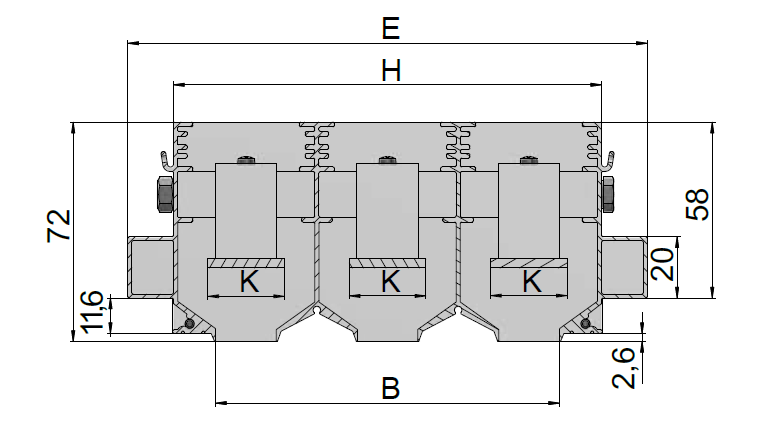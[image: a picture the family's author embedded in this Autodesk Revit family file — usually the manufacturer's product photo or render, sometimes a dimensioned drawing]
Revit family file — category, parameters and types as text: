
# Revit family: GR_Адаптер линейный_Муфта(n)_SDL-КСД-У_О_R21
name_source: partatom
category: Соединительные детали воздуховодов
units: mm (PartAtom-declared; Revit-internal decimal feet)

## family parameters
Всегда вертикально = Да
Заголовок OmniClass = Metal Ducts
На основе рабочей плоскости = Нет
Номер OmniClass = 23.75.70.14.31
Общий = Нет
При загрузке вырезать с полостями = Нет
Размер круглого соединителя = Использовать диаметр
Тип детали = Мультипорт

## types (6) — shared parameters
ADSK_URL страницы изделия = https://grilles.ru
ADSK_Версия Revit = 2021
ADSK_Единица измерения = шт.
ADSK_Завод-изготовитель = ООО "ВЕНТРЕШЕТКИКОМ"
ADSK_Код изделия = 000192
ADSK_Количество = 1
ADSK_Материал = ADSK_Оцинкованная сталь
ADSK_Наименование = SDL-КСД-У-О, адаптер вентиляционной решётки радиальный
Изготовитель = ООО "ВЕНТРЕШЕТКИКОМ"
Корпус_Металл_Толщина = 1 мм
Муфта_Металл_Толщина = 1 мм
zero-valued in all types: Отметка по умолчанию

## per-type parameters (varying)
| type | Корпус_Высота | Корпус_Длина | Решетка_отступ | Решётка_Высота |
| SDL-КСД-У-О 1-20 | 130 мм | 171 мм | 25 мм | 48 мм |
| SDL-КСД-У-О 2-20 | 130 мм | 209 мм | 44 мм | 86 мм |
| SDL-КСД-У-О 3-20 | 130 мм | 247 мм | 63 мм | 124 мм |
| SDL-КСД-У-О 4-20 | 170 мм | 285 мм | 82 мм | 162 мм |
| SDL-КСД-У-О 5-20 | 170 мм | 323 мм | 101 мм | 200 мм |
| SDL-КСД-У-О 6-20 | 170 мм | 361 мм | 120 мм | 238 мм |

note: column(s) folded — value = type name in every type: ADSK_Марка
